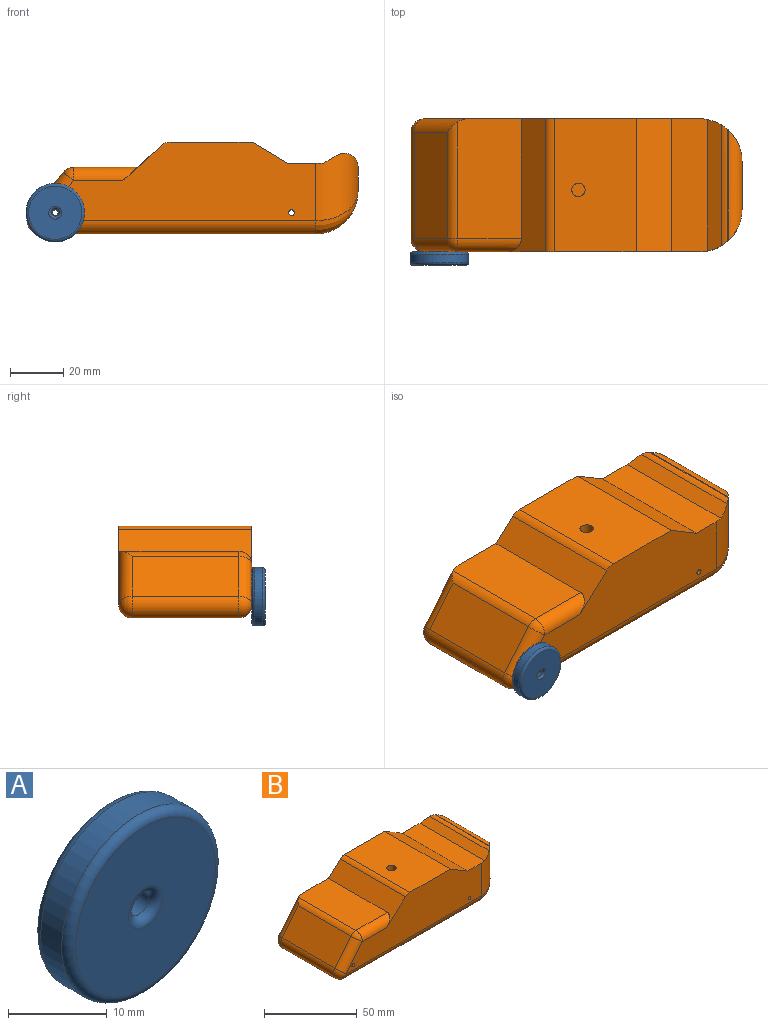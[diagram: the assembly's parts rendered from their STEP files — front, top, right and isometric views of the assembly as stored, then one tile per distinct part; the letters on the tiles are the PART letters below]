
ASSEMBLY  parts=2 mates=1
PART A: 8 faces, bbox 23.8x5x23.8 mm
  f0: cylinder r=1.43mm len=3mm, axis (0,1,0), area 26.9mm2, adj f4,f5
  f1: cylinder r=11mm len=22mm, axis (0,1,0), area 207.3mm2, adj f6,f7
  f2: plane 20x20mm, normal (0,-1,0), area 295.7mm2, adj f4,f6
  f3: plane 20x20mm, normal (0,1,0), area 295.7mm2, adj f5,f7
  f4: torus R=2.43mm, axis (0,-1,0), area 17.7mm2, adj f0,f2
  f5: torus R=2.43mm, axis (0,-1,0), area 17.7mm2, adj f0,f3
  f6: torus R=10mm, axis (0,-1,0), area 105mm2, adj f1,f2
  f7: torus R=10mm, axis (0,-1,0), area 105mm2, adj f1,f3
PART B: 39 faces, bbox 124.4x50.1x34.7 mm
  f0: plane 35.78x14.8mm, normal (1,0,0), area 529.5mm2, adj f1,f3,f4,f5
  f1: plane 22.15x14.8mm, normal (0,1,0), area 327.8mm2, adj f0,f2,f4,f5
  f2: plane 35.78x14.8mm, normal (-1,0,0), area 529.5mm2, adj f1,f3,f4,f5
  f3: plane 22.15x14.8mm, normal (0,-1,0), area 327.8mm2, adj f0,f2,f4,f5
  f4: plane 35.78x22.15mm, normal (0,0,1), area 792.6mm2, adj f0,f1,f2,f3
  f5: plane 35.78x22.15mm, normal (0,0,-1), area 772.9mm2, adj f0,f1,f2,f3,f6
  f6: cylinder r=2.5mm len=9.55mm, axis (0,0,1), area 150.1mm2, adj f5,f13
  f7: plane 103.41x40mm, normal (0,0,-1), area 4136.2mm2, adj f22,f23,f32,f36
  f8: plane 18.13x9.38mm, normal (1,0,0), area 170mm2, adj f29,f34,f36,f38
  f9: plane 41.87x0.3mm, normal (0,0,1), area 12.5mm2, adj f29,f30,f34,f38
  f10: plane 49.57x5.3mm, normal (-0.51,0,0.86), area 288.5mm2, adj f11,f30,f34,f38
  f11: plane 50x13.45mm, normal (0,0,1), area 672.1mm2, adj f10,f12,f19,f20,f34,f38
  f12: plane 50x13.3mm, normal (0.51,0,0.86), area 775.6mm2, adj f11,f13,f19,f20
  f13: plane 50x30.75mm, normal (0,0,1), area 1517.9mm2, adj f6,f12,f19,f20,f31
  f14: plane 50x14.41mm, normal (-0.68,0,0.74), area 616.8mm2, adj f15,f19,f20,f28,f31
  f15: plane 45x23.98mm, normal (0,0,1), area 1077.7mm2, adj f14,f20,f25,f26,f28
  f16: plane 40x15mm, normal (-0.77,0,0.64), area 780.3mm2, adj f21,f22,f25,f26
  f17: cylinder r=1.07mm len=50mm, axis (0,1,0), area 337.7mm2, adj f19,f20
  f18: cylinder r=1.07mm len=50mm, axis (0,1,0), area 337.7mm2, adj f19,f20
  f19: plane 103.41x29.55mm, normal (0,-1,0), area 2250.9mm2, adj f11,f12,f13,f14,f17,f18,f21,f28
  f20: plane 103.41x29.55mm, normal (0,1,0), area 2346.8mm2, adj f11,f12,f13,f14,f15,f17,f18,f23
  f21: cylinder r=5mm len=18.2mm, axis (0.64,0,0.77), area 153.2mm2, adj f16,f19,f27,f33
  f22: cylinder r=5mm len=40mm, axis (0,1,0), area 452.9mm2, adj f7,f16,f24,f33
  f23: cylinder r=5mm len=103.41mm, axis (1,0,0), area 812.1mm2, adj f7,f20,f24,f37
  f24: sphere r=5mm, area 56.6mm2, adj f22,f23,f25
  f25: cylinder r=5mm len=23.2mm, axis (-0.64,0,-0.77), area 180mm2, adj f15,f16,f20,f24,f26
  f26: cylinder r=5mm len=43.84mm, axis (0,1,0), area 184.4mm2, adj f15,f16,f25,f27
  f27: sphere r=5mm, area 21.9mm2, adj f21,f26,f28
  f28: cylinder r=5mm len=23.98mm, axis (1,0,0), area 172.8mm2, adj f14,f15,f19,f27
  f29: cylinder r=5mm len=41.31mm, axis (0,1,0), area 242.5mm2, adj f8,f9,f34,f38
  f30: cylinder r=5mm len=45.57mm, axis (0,1,0), area 116.4mm2, adj f9,f10,f34,f38
  f31: cylinder r=5mm len=50mm, axis (0,1,0), area 185.7mm2, adj f13,f14,f19,f20
  f32: cylinder r=5mm len=103.41mm, axis (-1,0,0), area 812.1mm2, adj f7,f19,f33,f35
  f33: sphere r=5mm, area 56.6mm2, adj f21,f22,f32
  f34: cylinder r=15.93mm len=25.31mm, axis (0,0,-1), area 485.2mm2, adj f8,f9,f10,f11,f19,f29,f30,f35
  f35: bspline ~16.62x15.93mm, area 133.8mm2, adj f32,f34,f36
  f36: cylinder r=15.93mm len=40mm, axis (0,1,0), area 802.3mm2, adj f7,f8,f35,f37
  f37: bspline ~16.62x15.93mm, area 133.8mm2, adj f23,f36,f38
  f38: cylinder r=15.93mm len=25.31mm, axis (0,0,1), area 485.2mm2, adj f8,f9,f10,f11,f20,f29,f30,f37
PLACE A t=(-99.7,-58.11,-17.28)mm
PLACE B t=(-37.25,-8.11,-0.28)mm
MATE fastened A.f0 <-> B.f17  axis (0,1,0) through (-99.7,-58.11,-17.28)mm
